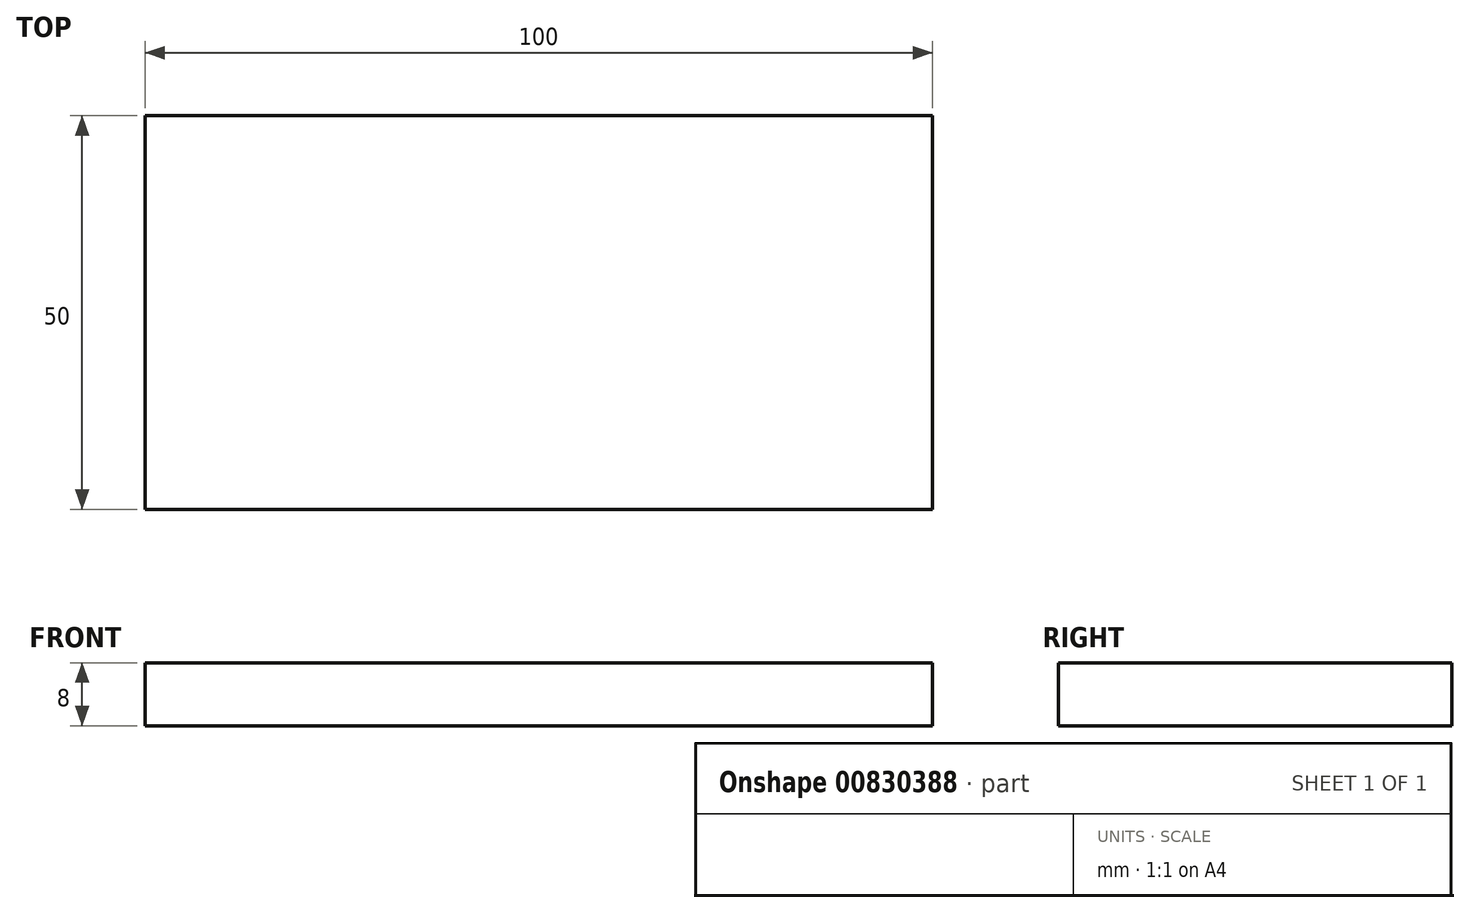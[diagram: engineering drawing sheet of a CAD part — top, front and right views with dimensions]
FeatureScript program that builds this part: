
annotation { "Feature Type Name" : "Feature", "Feature Type Description" : "" }
export const myFeature = defineFeature(function(context is Context, id is Id, definition is map)
    precondition{}
    {
        {
            var Q0;
            Q0=qCreatedBy(makeId("Top.planeOp"),FACE);
            var sketch = newSketch(context, id + "F0", { "sketchPlane" : qUnion([Q0])});
            skLineSegment(sketch, "E0.bottom", {"start": v(0, 0) * mm, "end": v(100, 0) * mm});
            skLineSegment(sketch, "E0.top", {"start": v(0, 50) * mm, "end": v(100, 50) * mm});
            skLineSegment(sketch, "E0.left", {"start": v(0, 0) * mm, "end": v(0, 50) * mm});
            skLineSegment(sketch, "E0.right", {"start": v(100, 0) * mm, "end": v(100, 50) * mm});
            skSolve(sketch);
        }
        {
            var Q0;
            Q0 = qSketchRegion(id + "F0", true);
            extrude(context, id + "F1", {"entities" : qUnion([Q0]), "depth" : 8 * mm, "offsetDistance" : 25 * mm});
        }
    });
